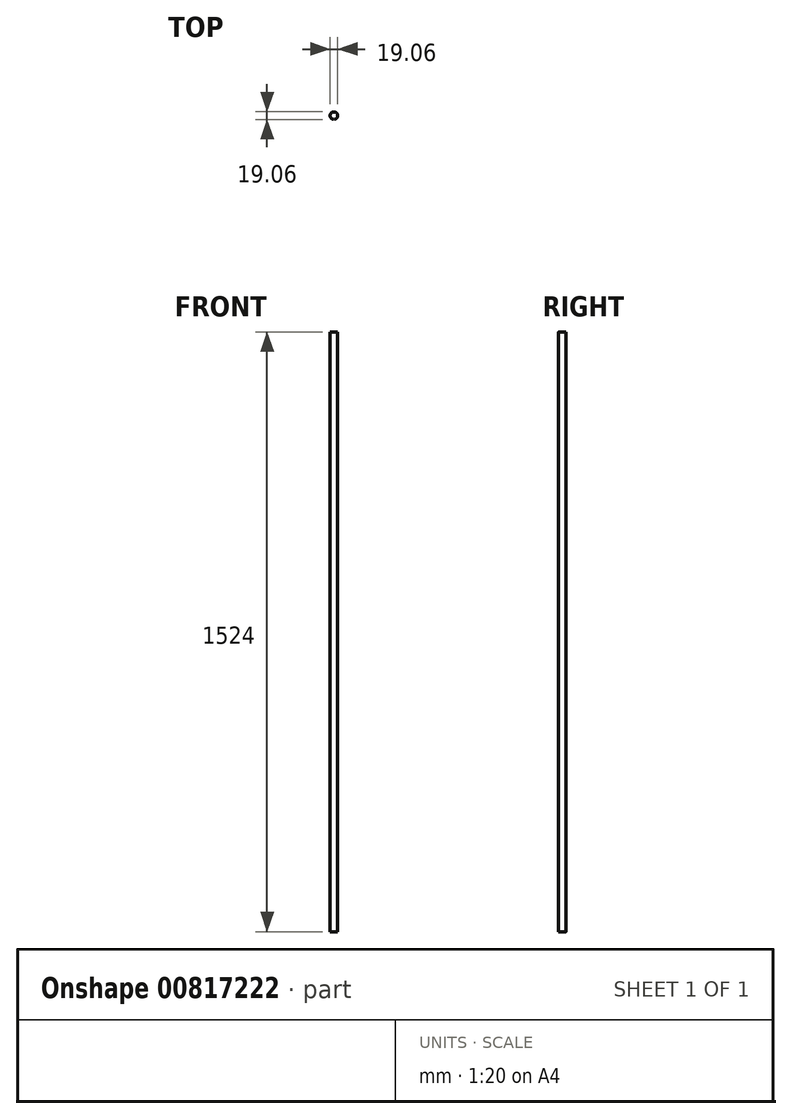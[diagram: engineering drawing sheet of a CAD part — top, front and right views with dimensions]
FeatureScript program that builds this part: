
annotation { "Feature Type Name" : "Feature", "Feature Type Description" : "" }
export const myFeature = defineFeature(function(context is Context, id is Id, definition is map)
    precondition{}
    {
        {
            var Q0;
            Q0=qCreatedBy(makeId("Top.planeOp"),FACE);
            var sketch = newSketch(context, id + "F0", { "sketchPlane" : qUnion([Q0])});
            skCircle(sketch, "E0", {"center": v(0, 0) * mm, "radius": 9.53 * mm});
            skSolve(sketch);
        }
        {
            var Q0;
            Q0=sQuery(id+"F0.wireOp",EDGE,"E0");
            extrude(context, id + "F1", {"bodyType" : ToolBodyType.SURFACE, "surfaceEntities" : qUnion([Q0]), "depth" : 1524 * mm, "offsetDistance" : 25.4 * mm});
        }
    });
